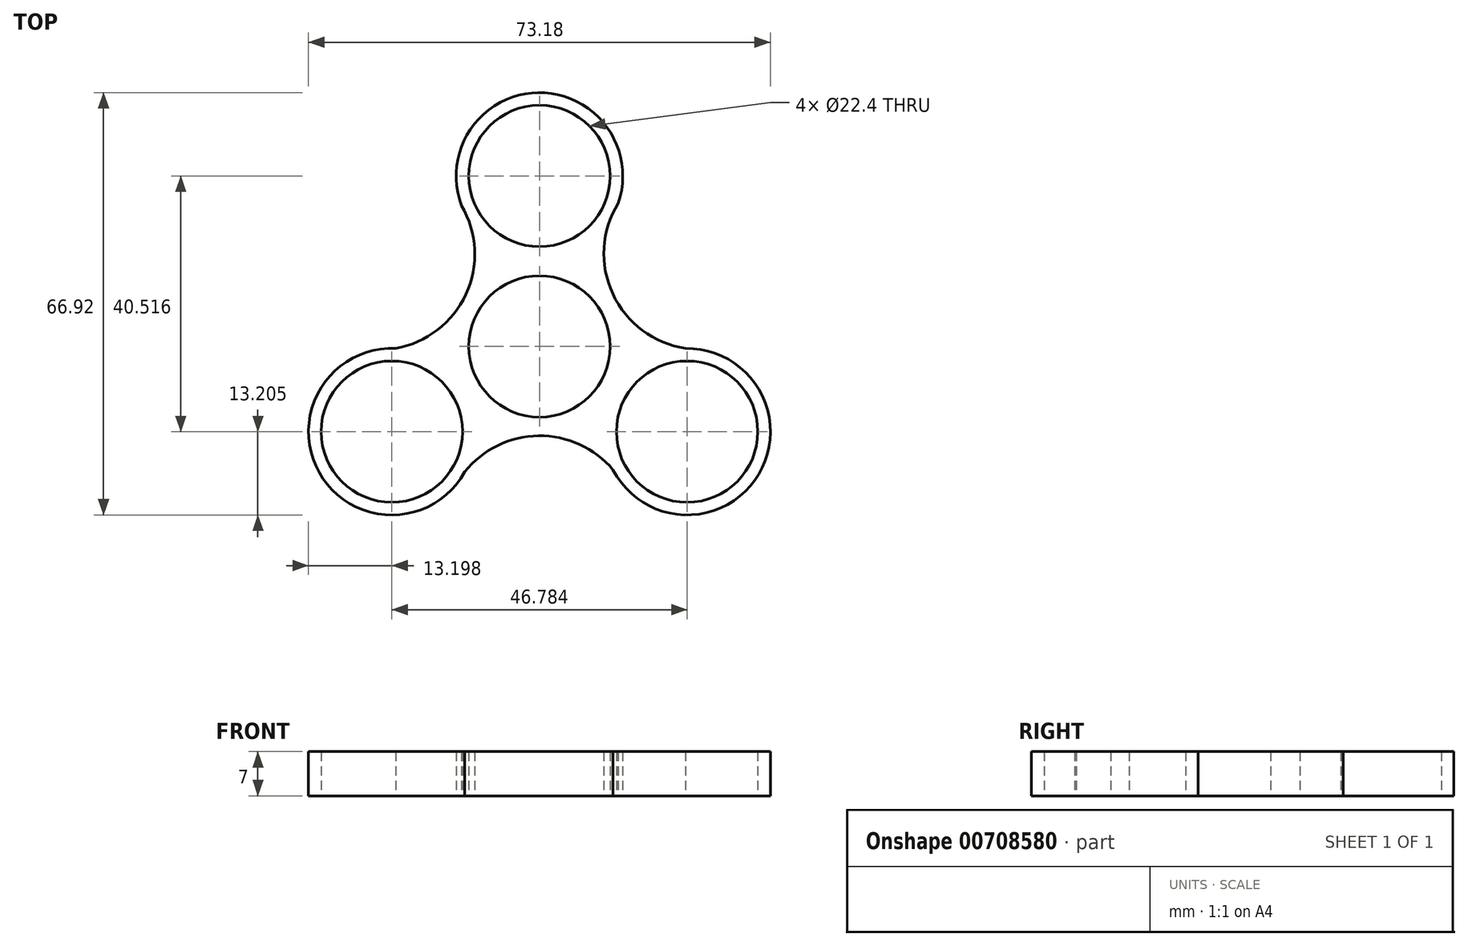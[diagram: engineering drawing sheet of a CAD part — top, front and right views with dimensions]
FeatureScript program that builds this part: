
annotation { "Feature Type Name" : "Feature", "Feature Type Description" : "" }
export const myFeature = defineFeature(function(context is Context, id is Id, definition is map)
    precondition{}
    {
        {
            var Q0;
            Q0=qCreatedBy(makeId("Top.planeOp"),FACE);
            var sketch = newSketch(context, id + "F0", { "sketchPlane" : qUnion([Q0])});
            skCircle(sketch, "E0", {"center": v(0, 0) * mm, "radius": 11.2 * mm});
            skCircle(sketch, "E1", {"center": v(0, 27.01) * mm, "radius": 11.2 * mm});
            skArc(sketch, "E2", {"start": v(10.7, 19.29) * mm, "mid": v(10.92, 19.6) * mm, "end": v(11.12, 19.9) * mm});
            skArc(sketch, "E3.1.0", {"start": v(-22.8, -0.32) * mm, "mid": v(-34.91, -19.95) * mm, "end": v(-11.84, -19.89) * mm});
            skCircle(sketch, "E3.1.1", {"center": v(-23.4, -13.5) * mm, "radius": 11.2 * mm});
            skArc(sketch, "E3.2.0", {"start": v(11.67, -19.58) * mm, "mid": v(34.73, -20.26) * mm, "end": v(23.14, -0.3) * mm});
            skCircle(sketch, "E3.2.1", {"center": v(23.4, -13.5) * mm, "radius": 11.2 * mm});
            skArc(sketch, "E4", {"start": v(13.42, -22.15) * mm, "mid": v(0.22, -14.16) * mm, "end": v(-13.16, -21.85) * mm});
            skPoint(sketch, "E5.start.orphan", {"position": v(-23.4, -0.3) * mm});
            skArc(sketch, "E6.1.0", {"start": v(12.48, 22.7) * mm, "mid": v(12.16, 7.27) * mm, "end": v(25.5, -0.48) * mm});
            skArc(sketch, "E6.2.0", {"start": v(-25.9, -0.54) * mm, "mid": v(-12.37, 6.9) * mm, "end": v(-12.34, 22.32) * mm});
            skArc(sketch, "E7.trimOffspring", {"start": v(12.48, 22.7) * mm, "mid": v(-0.2, 40.2) * mm, "end": v(-12.34, 22.32) * mm});
            skSolve(sketch);
        }
        {
            var Q0;
            Q0 = qSketchRegion(id + "F0", true);
            extrude(context, id + "F1", {"entities" : qUnion([Q0]), "depth" : 7 * mm, "offsetDistance" : 25 * mm});
        }
    });
